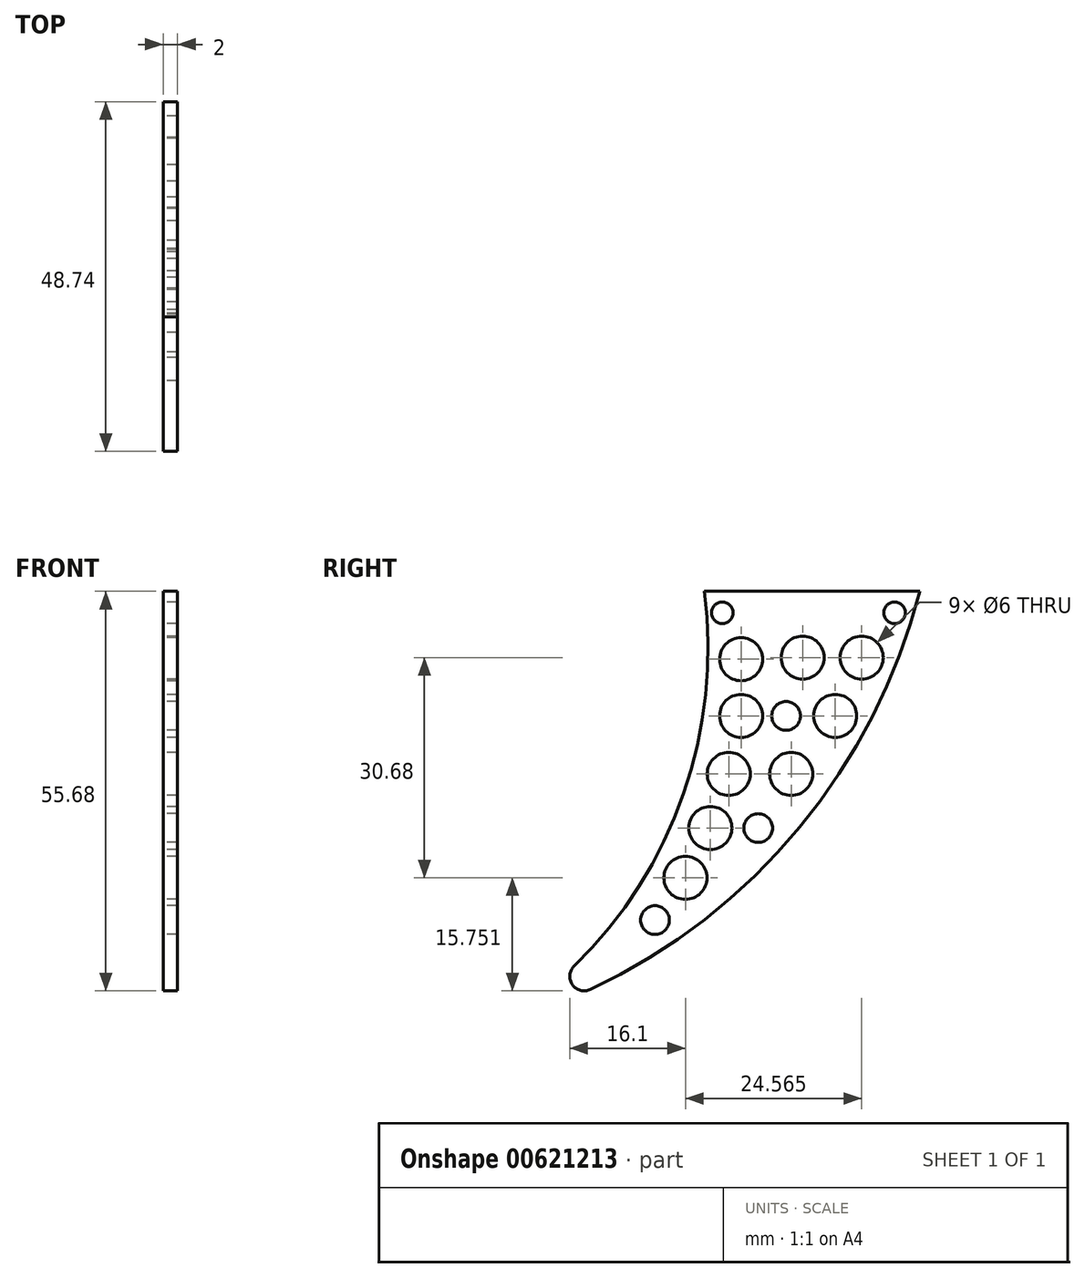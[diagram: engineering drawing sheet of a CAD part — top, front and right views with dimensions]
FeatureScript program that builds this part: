
annotation { "Feature Type Name" : "Feature", "Feature Type Description" : "" }
export const myFeature = defineFeature(function(context is Context, id is Id, definition is map)
    precondition{}
    {
        {
            var Q0;
            Q0=qCreatedBy(makeId("Right.planeOp"),FACE);
            var sketch = newSketch(context, id + "F0", { "sketchPlane" : qUnion([Q0])});
            skLineSegment(sketch, "E0", {"start": v(-16.6, 15.51) * mm, "end": v(13.4, 15.51) * mm});
            skArc(sketch, "E1", {"start": v(-44.55, -44.55) * mm, "mid": v(-7.62, -22.19) * mm, "end": v(13.4, 15.51) * mm});
            skArc(sketch, "E2", {"start": v(-44.55, -44.55) * mm, "mid": v(-21.87, -18.57) * mm, "end": v(-16.6, 15.51) * mm});
            skCircle(sketch, "E3", {"center": v(-14.1, 12.51) * mm, "radius": 1.5 * mm});
            skCircle(sketch, "E4", {"center": v(9.9, 12.51) * mm, "radius": 1.5 * mm});
            skCircle(sketch, "E5", {"center": v(-11.47, 6.04) * mm, "radius": 3 * mm});
            skCircle(sketch, "E6", {"center": v(-11.47, -1.86) * mm, "radius": 3 * mm});
            skCircle(sketch, "E7", {"center": v(-13.2, -9.94) * mm, "radius": 3 * mm});
            skCircle(sketch, "E8", {"center": v(-15.76, -17.49) * mm, "radius": 3 * mm});
            skCircle(sketch, "E9", {"center": v(-19.24, -24.42) * mm, "radius": 3 * mm});
            skCircle(sketch, "E10", {"center": v(-23.48, -30.3) * mm, "radius": 2 * mm});
            skCircle(sketch, "E11", {"center": v(5.33, 6.26) * mm, "radius": 3 * mm});
            skCircle(sketch, "E12", {"center": v(-2.9, 6.26) * mm, "radius": 3 * mm});
            skCircle(sketch, "E13", {"center": v(-4.5, -9.94) * mm, "radius": 3 * mm});
            skCircle(sketch, "E14", {"center": v(1.63, -1.86) * mm, "radius": 3 * mm});
            skCircle(sketch, "E15", {"center": v(-5.21, -1.86) * mm, "radius": 2 * mm});
            skCircle(sketch, "E16", {"center": v(-9.1, -17.49) * mm, "radius": 2 * mm});
            skSolve(sketch);
        }
        {
            var Q0;
            Q0 = qSketchRegion(id + "F0", true);
            extrude(context, id + "F1", {"entities" : qUnion([Q0]), "depth" : 2 * mm, "offsetDistance" : 25 * mm});
        }
        {
            var Q0;
            Q0=makeQuery(id+"F1.opExtrude","SWEPT_EDGE",EDGE,{"disambiguationData":[OSD([sQuery(id+"F0.wireOp",EDGE,"E1"),sQuery(id+"F0.wireOp",EDGE,"E2")])]});
            fillet(context, id + "F2", {"entities" : qUnion([Q0]), "radius" : 2 * mm, "tangentPropagation" : true, "allowEdgeOverflow" : false});
        }
    });
